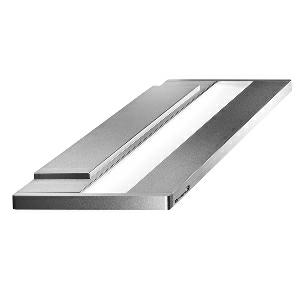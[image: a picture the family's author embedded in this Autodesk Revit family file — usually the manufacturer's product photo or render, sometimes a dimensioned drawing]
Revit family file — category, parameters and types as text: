
# Revit family: zera_bed_-_zew_9000_830_-_ul_nl_00812991_537b
name_source: partatom
category: Lighting Fixtures
units: mm (PartAtom-declared; Revit-internal decimal feet)

## family parameters
Cut with Voids When Loaded = No
Host = Face
Light Source = No
Part Type = Normal
Room Calculation Point = No
Round Connector Dimension = Use Diameter
Shared = No

## types (1)
- AL+UL (1 x LED, 7600 lm, 4000K/3000K)
    Apparent Load = 76 VA
    Approval mark = CE
    CIE Flux Codes = 45 81 99 31 100
    Color Rendering = 90/80
    Color Temperature = 4000K/3000K
    Default Elevation = 2000 mm  [stored 6.56168 ft]
    Description = ZEW 9000/830|Wall-mounted luminaire|light source:   Warm white   |work equipment: Power supply unit|luminous flux: 8960 lm|light distribution: Direct/indirect|class of protection: I|technology: Switchable|mains lead: Connector 5 pin|glare control: Diffusor|special features: General light, indirect, 3000K, Ra80, DIN EN 60598-2-25, Reading light, direct, 2700K, Ra90, indir, dir 4K 36W Ra95|
    Frequency = 50 Hz, 60 Hz
    Height = 20 mm  [stored 0.0656168 ft]
    Lamp = 1 x LED
    Lamp Light Flux = 7600 lm
    Lamp count = 1
    Length = 1050 mm
    Luminous efficacy = 100 lm/W
    Manufacturer = Waldmann
    ModVariant = No
    Model = 00812991
    Mounting Place = Wall
    Mounting Type = Surface mounted
    Number of Poles = 1
    OnlyDefault = Yes
    Power Factor = 1
    Product Name = ZERA.bed - ZEW 9000/830 - UL/NL
    Product group = Wall mounted Luminaire
    ProductGroupID = 20
    Protection Class = Protection class I
    Protection Degree = IP 20
    RLX_Detail_Level = 1
    RLX_Emergency_Light_Flux = 0 lm
    RLX_Emergency_Type = 0
    RLX_Emergency_Type_DB = No
    RlxData = <blob elided: 62617 chars, md5=bd66ded1>
    Socket = socket
    Standby Power = 0 W
    System Light Flux = 7600 lm
    System Power = 76 W
    Type Comments = General and Examation Light
    Type Image = zera_bed.jpg
    URL = http://relux.com
    VarID = al_ul_37f9
    Voltage = 230 V
    Voltage Range = 220-240 V
    Weight = 0.00 kg
    Width = 230 mm

note: [stored X ft] marks values corroborated as IEEE doubles in the binary element streams (Revit-internal decimal feet)

## geometry (parser evidence)
native form markers: Blend x4, Sweep x12
no freeform markers — native parametric forms only
